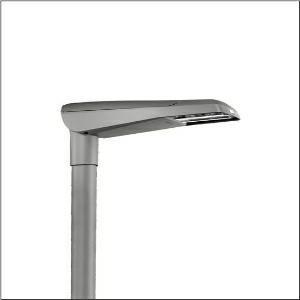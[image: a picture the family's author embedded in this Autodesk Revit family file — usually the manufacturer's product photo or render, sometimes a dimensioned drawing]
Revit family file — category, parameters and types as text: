
# Revit family: streetlight_sl_11_iq_micro___st0_5a_5xc1b51f08ce_ff99
name_source: partatom
category: Lighting Fixtures
units: mm (PartAtom-declared; Revit-internal decimal feet)

## family parameters
Cut with Voids When Loaded = No
Host = Face
Light Source = No
Part Type = Normal
Room Calculation Point = No
Round Connector Dimension = Use Diameter
Shared = No

## types (1)
- --- (1 x LED, 1860 lm, 12.6 W, 3000K)
    Apparent Load = 13 VA
    CIE Flux Codes = 42 72 97 100 100
    Color Rendering = 70
    Color Temperature = 3000K
    Default Elevation = 1800 mm
    Description = Streetlight SL 11 iQ micro, mast luminaire, primary light control with 3 zone facetted reflector, of plastic, silver coated, highly specular, primary optical cover: cover, of PMMA, transparent, light distribution: ST0.5a, light emission: direct distribution, primary light characteristic: asymmetric, installation type: post-top, side-entry, lamps: LED, High Power LED, rated values: 1.860lm | 12,6W | 147,6lm/W (begin service life); end service life: 1.860lm | 12,9W; at 50% lumin. flux: 930lm | 6,8W | 136,8lm/W, colour temperature: 3000K, colour rendering: CRI > 70, light colour: 730, light setting 1 begin service life: 100% | 1.860lm | 12,6W | 147,6lm/W | 3.000K, light setting 1 end service life: 12,9W, further light settings possible, control: Street-Remote, optimised constant luminous flux control (CLO 2.0), Desk-Remote (wireless, voltage-free reading and setting of iQ features in the workshop via application-optimized NFC function/RFID function), Light-Fading, Smart-Wire, Night-Set, Lumen-Switch, Temp-Guard, Auto-Match, with cable H07RN-F 3x 1.5mm², mains connection: 230..240V, AC, 50/60Hz, connection cable pre-assembled, cable length: 5,5m, luminaire housing, of diecast aluminium, powder-coated, SITECO metallic grey (DB 702S), please order mast flange separately, inclination adjustable without tools: 0°, 5°, 10°, 15° (post-top) | 0°, -5°, -10°, -15° (side-entry), sealing non-destructively replaceable, multi-level sealing system, length: 600mm, width: 174mm, height: 116mm, mast flange for spigot size: 42mm (side-entry): 5XC10008XM4, 60/48mm (side-entry/post-top): 5XC10108XM2, 76/60mm (side-entry/post-top): 5XC10108XM1, equipment: standard, protection rating (complete): IP66, insulation class (complete): insulation class II (safety insulation), certification: CE, ENEC, ENEC+, VDE, impact resistance: IK10, permissible operating ambient temperature for outdoor applications: -25..+50°C, standard-compliant lighting for roads and squares, Environmental Product Declaration (EPD) tested and certified by an independent institute, packaging unit: 1 piece

Light Distribution: ST0.5a
    Height = 116 mm
    Lamp = 1 x LED
    Lamp Light Flux = 1860 lm
    Lamp Power = 12.6 W
    Lamp count = 1
    Length = 600 mm
    Luminous efficacy = 148 lm/W
    Manufacturer = Siteco
    ModVariant = No
    Model = 5XC1B51F08CE
    Number of Poles = 1
    OnlyDefault = Yes
    Power Factor = 1
    Product Name = Streetlight SL 11 iQ micro | ST0.5a
    Product group = mast luminaire | pylon top
    ProductGroupID = 6100
    Protection Class = Protection class II
    Protection Degree = IP 66
    RLX_Detail_Level = 1
    RLX_Emergency_Light_Flux = 0 lm
    RLX_Emergency_Type = 0
    RLX_Emergency_Type_DB = No
    RlxData = <blob elided: 26781 chars, md5=18fa812a>
    Socket = socket
    Standby Power = 0 W
    System Light Flux = 1860 lm
    System Power = 13 W
    Type Comments = factory setting: luminous flux: 100 % | dim-lin: 254 | 229 mA
    Type Image = l_1006566.jpg
    URL = http://relux.com
    VarID = @adj_021751
    Voltage = 0 V
    Weight = 0.00 kg
    Width = 174 mm

## geometry (parser evidence)
native form markers: Blend x4, Sweep x9
no freeform markers — native parametric forms only
